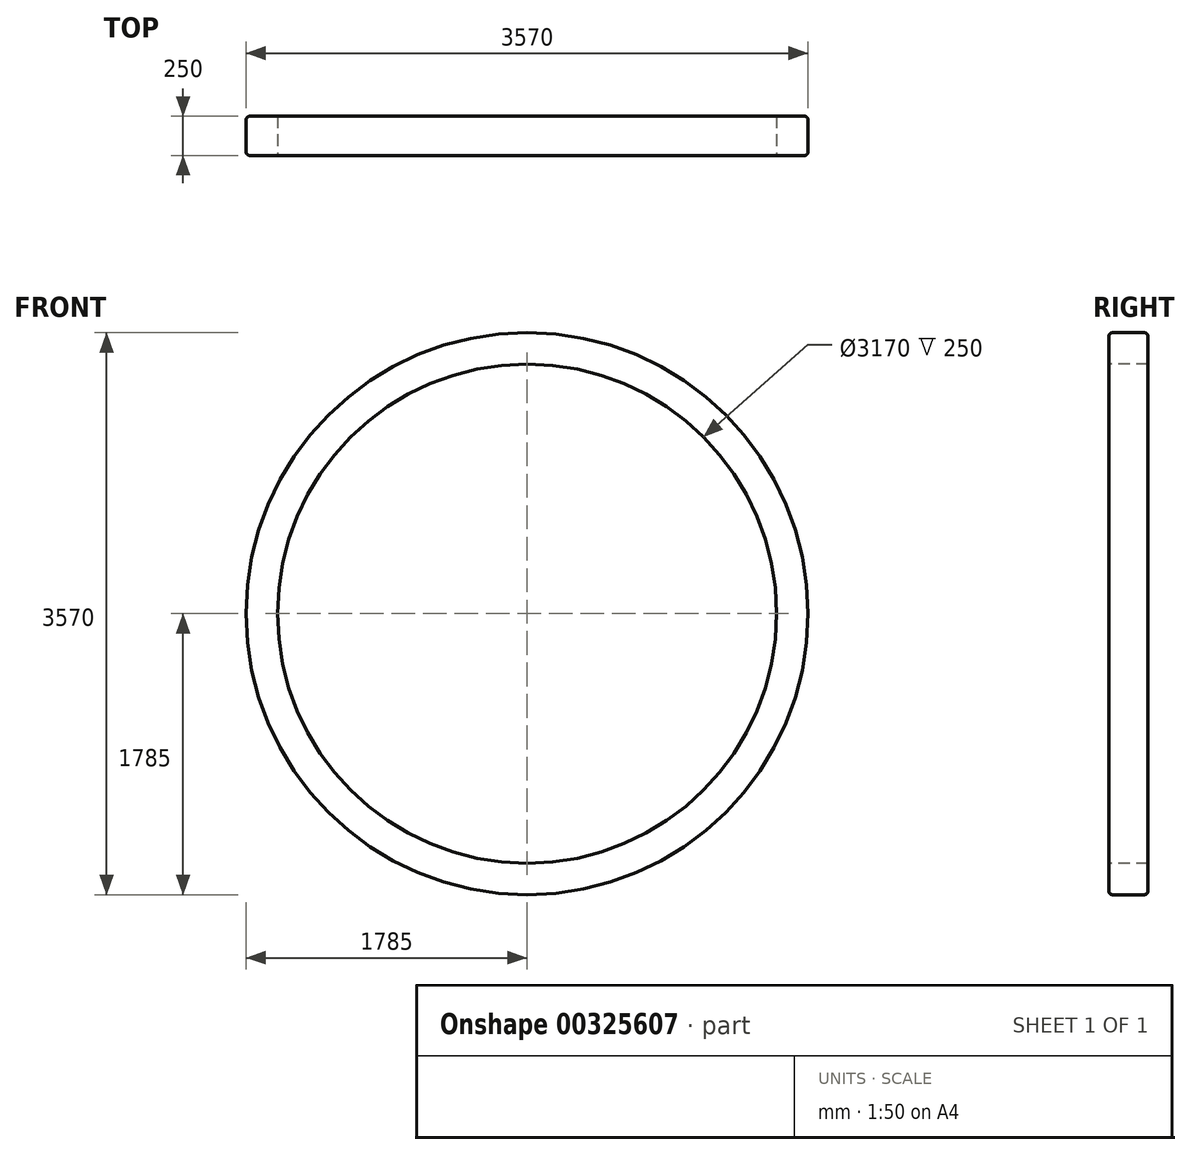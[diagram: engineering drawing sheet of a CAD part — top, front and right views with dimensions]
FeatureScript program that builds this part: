
annotation { "Feature Type Name" : "Feature", "Feature Type Description" : "" }
export const myFeature = defineFeature(function(context is Context, id is Id, definition is map)
    precondition{}
    {
        {
            var Q0;
            Q0=qCreatedBy(makeId("Right.planeOp"),FACE);
            var sketch = newSketch(context, id + "F0", { "sketchPlane" : qUnion([Q0])});
            skLineSegment(sketch, "E0.bottom", {"start": v(125, 1585) * mm, "end": v(-125, 1585) * mm});
            skLineSegment(sketch, "E0.top", {"start": v(100, 1785) * mm, "end": v(-100, 1785) * mm});
            skLineSegment(sketch, "E0.left", {"start": v(125, 1585) * mm, "end": v(125, 1760) * mm});
            skLineSegment(sketch, "E0.right", {"start": v(-125, 1585) * mm, "end": v(-125, 1760) * mm});
            skPoint(sketch, "E0.middle", {"position": v(0, 1685) * mm});
            skPoint(sketch, "E1.visualSharp", {"position": v(-125, 1785) * mm});
            skArc(sketch, "E1.filletArc", {"start": v(-100, 1785) * mm, "mid": v(-117.68, 1777.68) * mm, "end": v(-125, 1760) * mm});
            skPoint(sketch, "E2.visualSharp", {"position": v(125, 1785) * mm});
            skArc(sketch, "E2.filletArc", {"start": v(125, 1760) * mm, "mid": v(117.68, 1777.68) * mm, "end": v(100, 1785) * mm});
            skLineSegment(sketch, "E3", {"start": v(-75.44, 0) * mm, "end": v(74.7, 0) * mm, "construction": true});
            skSolve(sketch);
        }
        {
            var Q0;
            Q0=makeQuery(id+"F0.imprint","IMPRINT",FACE,{"disambiguationData":[TD([[makeQuery(id+"F0.imprint","IMPRINT",EDGE,{"derivedFrom":sQuery(id+"F0.wireOp",EDGE,"E0.bottom")}),-1.0]])]});
            var Q1;
            Q1=sQuery(id+"F0.wireOp",EDGE,"E3");
            revolve(context, id + "F1", {"entities" : qUnion([Q0]), "axis" : qUnion([Q1]), "revolveType" : RevolveType.FULL});
        }
    });
